# Revit family: Building-IEC309Connections-GEWISS-IEC309HP-10°_FLUSH-MOUNT_SOCKET_63A_IP44-54
name_source: partatom
category: Apparecchi elettrici
units: mm (PartAtom-declared; Revit-internal decimal feet)

## family parameters
Condiviso = Sì
Host = Superficie
Mantenere orientamento annotazione = Sì
Punto di calcolo locali = Sì
Quota connettore circolare = Usa diametro
Taglio con vuoti quando caricato = No
Tipo di parte = Normale

## types (9) — shared parameters
BLOCCO = B=C
Breaking capacity at 1.1 Un = 79A
Catalogue = BUILDING
Corpo centrale = Default(2)
Electrocod = 2210
FORMULA = 1000 mm  [stored 3.28084 ft]
Flange dimensions (mm) = 110x100
Frequency = 50/60 Hz
Glow wire test: = 850 °C (active parts) - 650 °C (passive parts)
IDF = f1048570-cea4-440a-a8ba-56aa143d5f84
IDT = bd500f5bebc94172aa8bf80527fc28cd
IP degree = IP44/IP54
Immagine tipo = <Nessuno>
Insulation resistance = - 10 M?
L = 155 mm
Operating temperature: = -25 +55 °C
Piastra = Default(2)
Produttore = GEWISS S.p.A.
Prospetto di default = 500 mm
Rated current (A) = 63
SEO = Socket outlet
SPinotto = Default(2)
Shock resistance = IK09
Sportello_visibile = Sì
Spostamento_S = 950 mm
Technical sheet = https://www.gewiss.com
Terminal tightening capacity = 6-16mm² flexible cables - 6-25mm² rigid cables
Thermo-pressure with ball = 125 °C (active parts) - 80 °C (passive parts)
Total number of operations = -2000
Type of material = Halogen-free in compliance with EN 60754-2
Type of wiring = Mantle terminal
Typology = 10° angled flush-mounting socket-outlet
URL = https://www.gewiss.com
Version file RFA = 21.11
W = 115 mm

## per-type parameters (varying)
| type | Colour: | Descrizione | Modello | No. of poles | Rated voltage: | Reference h |
| GW63220H - 10°FLUSH.S.O.HP IP44 3P+E 63A 400V 6H | Red | 10°FLUSH.S.O.HP IP44 3P+E 63A 400V 6H | GW63220H | 3P+E | 380 - 415 V | 6 |
| GW63213H - 10°FLUSH.S.O.HP IP44 2P+E 63A 110V 4H | Yellow | 10°FLUSH.S.O.HP IP44 2P+E 63A 110V 4H | GW63213H | 2P+E | 100 - 130 V | 4 |
| GW63216H - 10°FLUSH.S.O.HP IP44 2P+E 63A 230V 6H | Blue | 10°FLUSH.S.O.HP IP44 2P+E 63A 230V 6H | GW63216H | 2P+E | 200 - 250 V | 6 |
| GW63214H - 10°FLUSH.S.O.HP IP44 3P+E 63A 110V 4H | Yellow | 10°FLUSH.S.O.HP IP44 3P+E 63A 110V 4H | GW63214H | 3P+E | 100 - 130 V | 4 |
| GW63221H - 10°FLUSH.S.O.HP IP44 3P+N+E 63A 400V 6H | Red | 10°FLUSH.S.O.HP IP44 3P+N+E 63A 400V 6H | GW63221H | 3P+N+E | 346 - 415 V | 6 |
| GW63218H - 10°FLUSH.S.O.HP IP44 3P+N+E 63A 230V 9H | Blue | 10°FLUSH.S.O.HP IP44 3P+N+E 63A 230V 9H | GW63218H | 3P+N+E | 200 - 250 V | 9 |
| GW63219H - 10°FLUSH.S.O.HP IP44 2P+E 63A 400V 9H | Red | 10°FLUSH.S.O.HP IP44 2P+E 63A 400V 9H | GW63219H | 2P+E | 380 - 415 V | 9 |
| GW63215H - 10°FLUSH.S.O.HP IP44 3P+N+E 63A 110V 4H | Yellow | 10°FLUSH.S.O.HP IP44 3P+N+E 63A 110V 4H | GW63215H | 3P+N+E | 100 - 130 V | 4 |
| GW63217H - 10°FLUSH.S.O.HP IP44 3P+E 63A 230V 9H | Blue | 10°FLUSH.S.O.HP IP44 3P+E 63A 230V 9H | GW63217H | 3P+E | 200 - 250 V | 9 |

note: [stored X ft] marks values corroborated as IEEE doubles in the binary element streams (Revit-internal decimal feet)

## geometry (parser evidence)
native form markers: Sweep x1
no freeform markers — native parametric forms only
